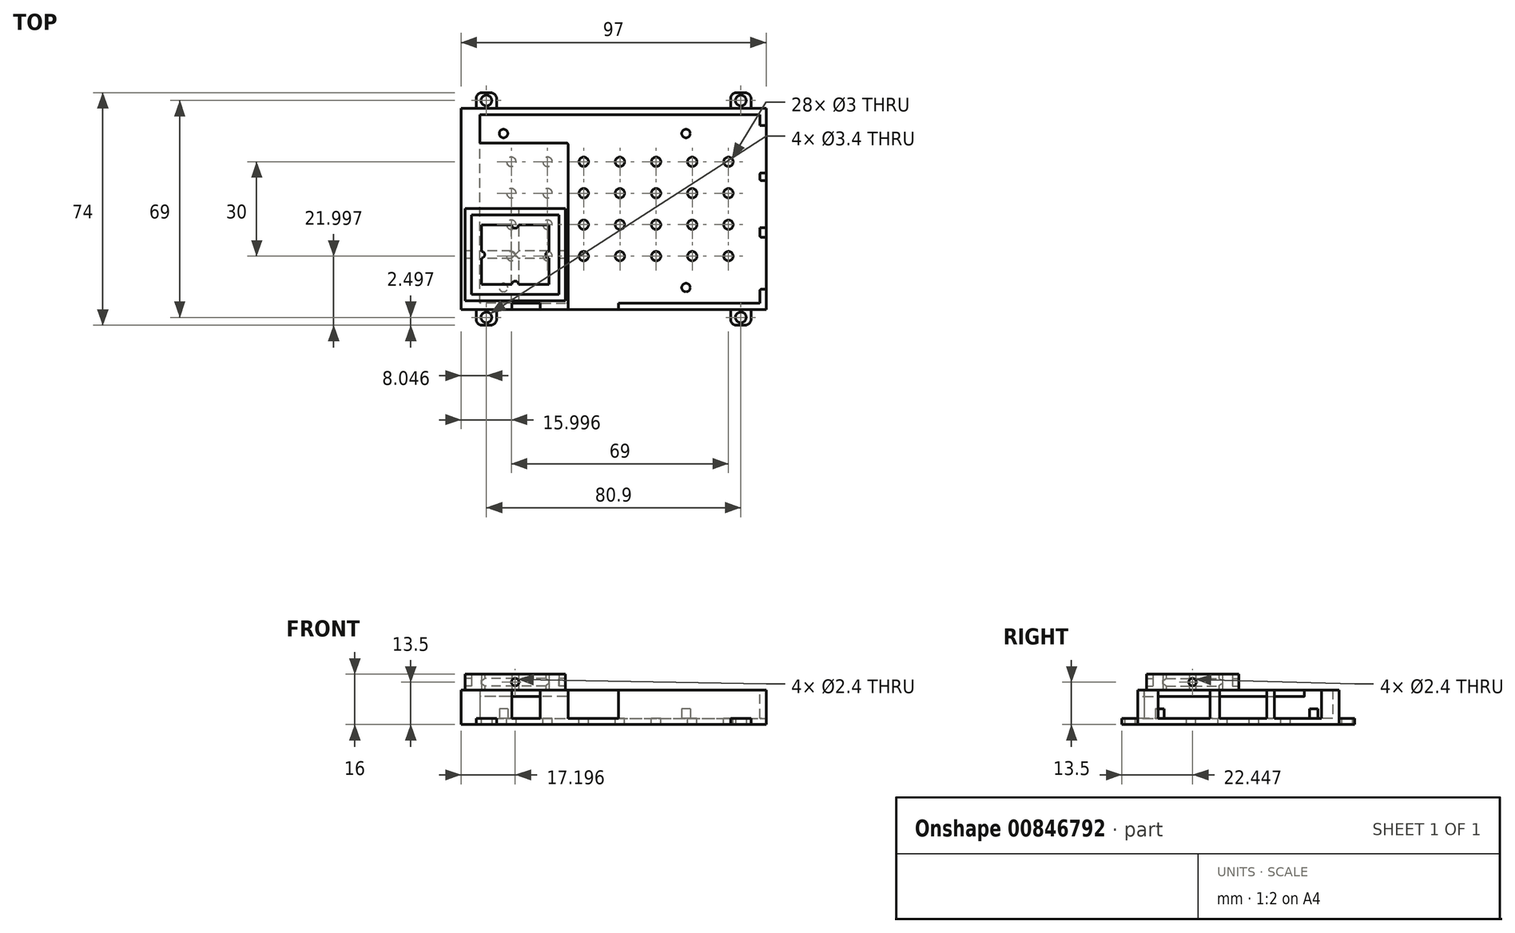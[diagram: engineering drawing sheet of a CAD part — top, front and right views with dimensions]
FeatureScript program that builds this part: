
annotation { "Feature Type Name" : "Feature", "Feature Type Description" : "" }
export const myFeature = defineFeature(function(context is Context, id is Id, definition is map)
    precondition{}
    {
        {
            var Q0;
            Q0=qCreatedBy(makeId("Top.planeOp"),FACE);
            var sketch = newSketch(context, id + "F0", { "sketchPlane" : qUnion([Q0])});
            skLineSegment(sketch, "E0.bottom", {"start": v(-40.08, 52.72) * mm, "end": v(56.92, 52.72) * mm});
            skLineSegment(sketch, "E0.top", {"start": v(-40.08, -11.28) * mm, "end": v(56.92, -11.28) * mm});
            skLineSegment(sketch, "E0.left", {"start": v(-40.08, 52.72) * mm, "end": v(-40.08, -11.28) * mm});
            skLineSegment(sketch, "E0.right", {"start": v(56.92, 52.72) * mm, "end": v(56.92, -11.28) * mm});
            skLineSegment(sketch, "E1", {"start": v(-34.08, 52.72) * mm, "end": v(-34.08, -11.28) * mm});
            skLineSegment(sketch, "E2", {"start": v(-40.08, -9.28) * mm, "end": v(56.92, -9.28) * mm});
            skLineSegment(sketch, "E3", {"start": v(54.92, -11.28) * mm, "end": v(54.92, 52.72) * mm});
            skLineSegment(sketch, "E4", {"start": v(-40.08, 50.72) * mm, "end": v(56.92, 50.72) * mm});
            skCircle(sketch, "E5", {"center": v(-26.58, 44.72) * mm, "radius": 1.35 * mm});
            skCircle(sketch, "E6", {"center": v(31.42, 44.72) * mm, "radius": 1.35 * mm});
            skCircle(sketch, "E7", {"center": v(31.42, -4.28) * mm, "radius": 1.35 * mm});
            skCircle(sketch, "E8", {"center": v(-26.58, -4.28) * mm, "radius": 1.35 * mm});
            skSolve(sketch);
        }
        {
            var Q0;
            {var subQ0=sQuery(id+"F0.wireOp",EDGE,"E2");var subQ1=sQuery(id+"F0.wireOp",EDGE,"E0.left");var subQ2=makeQuery(id+"F0.imprint","INTERSECT",VERTEX,{"derivedFrom":[subQ1,subQ0]});Q0=makeQuery(id+"F0.imprint","IMPRINT",FACE,{"disambiguationData":[TD([[makeQuery(id+"F0.imprint","IMPRINT",EDGE,{"disambiguationData":[TD([[subQ2,1.0]])],"derivedFrom":subQ1}),1.0]])]});}
            var Q1;
            {var subQ0=sQuery(id+"F0.wireOp",EDGE,"E1");var subQ1=sQuery(id+"F0.wireOp",EDGE,"E0.bottom");var subQ2=makeQuery(id+"F0.imprint","INTERSECT",VERTEX,{"derivedFrom":[subQ1,subQ0]});Q1=makeQuery(id+"F0.imprint","IMPRINT",FACE,{"disambiguationData":[TD([[makeQuery(id+"F0.imprint","IMPRINT",EDGE,{"disambiguationData":[TD([[subQ2,-1.0]])],"derivedFrom":subQ1}),-1.0]])]});}
            var Q2;
            {var subQ0=sQuery(id+"F0.wireOp",EDGE,"E1");var subQ1=sQuery(id+"F0.wireOp",EDGE,"E0.top");var subQ2=makeQuery(id+"F0.imprint","INTERSECT",VERTEX,{"derivedFrom":[subQ1,subQ0]});Q2=makeQuery(id+"F0.imprint","IMPRINT",FACE,{"disambiguationData":[TD([[makeQuery(id+"F0.imprint","IMPRINT",EDGE,{"disambiguationData":[TD([[subQ2,-1.0]])],"derivedFrom":subQ1}),1.0]])]});}
            var Q3;
            {var subQ0=sQuery(id+"F0.wireOp",EDGE,"E0.left");var subQ1=sQuery(id+"F0.wireOp",EDGE,"E0.top");var subQ2=makeQuery(id+"F0.imprint","INTERSECT",VERTEX,{"derivedFrom":[subQ1,subQ0]});Q3=makeQuery(id+"F0.imprint","IMPRINT",FACE,{"disambiguationData":[TD([[makeQuery(id+"F0.imprint","IMPRINT",EDGE,{"disambiguationData":[TD([[subQ2,-1.0]])],"derivedFrom":subQ1}),1.0]])]});}
            var Q4;
            {var subQ0=sQuery(id+"F0.wireOp",EDGE,"E0.left");var subQ1=sQuery(id+"F0.wireOp",EDGE,"E0.bottom");var subQ2=makeQuery(id+"F0.imprint","INTERSECT",VERTEX,{"derivedFrom":[subQ1,subQ0]});Q4=makeQuery(id+"F0.imprint","IMPRINT",FACE,{"disambiguationData":[TD([[makeQuery(id+"F0.imprint","IMPRINT",EDGE,{"disambiguationData":[TD([[subQ2,-1.0]])],"derivedFrom":subQ1}),-1.0]])]});}
            var Q5;
            {var subQ0=sQuery(id+"F0.wireOp",EDGE,"E0.right");var subQ1=sQuery(id+"F0.wireOp",EDGE,"E0.bottom");var subQ2=makeQuery(id+"F0.imprint","INTERSECT",VERTEX,{"derivedFrom":[subQ1,subQ0]});Q5=makeQuery(id+"F0.imprint","IMPRINT",FACE,{"disambiguationData":[TD([[makeQuery(id+"F0.imprint","IMPRINT",EDGE,{"disambiguationData":[TD([[subQ2,1.0]])],"derivedFrom":subQ1}),-1.0]])]});}
            var Q6;
            {var subQ0=sQuery(id+"F0.wireOp",EDGE,"E2");var subQ1=sQuery(id+"F0.wireOp",EDGE,"E0.right");var subQ2=makeQuery(id+"F0.imprint","INTERSECT",VERTEX,{"derivedFrom":[subQ1,subQ0]});Q6=makeQuery(id+"F0.imprint","IMPRINT",FACE,{"disambiguationData":[TD([[makeQuery(id+"F0.imprint","IMPRINT",EDGE,{"disambiguationData":[TD([[subQ2,1.0]])],"derivedFrom":subQ1}),-1.0]])]});}
            var Q7;
            {var subQ0=sQuery(id+"F0.wireOp",EDGE,"E0.right");var subQ1=sQuery(id+"F0.wireOp",EDGE,"E0.top");var subQ2=makeQuery(id+"F0.imprint","INTERSECT",VERTEX,{"derivedFrom":[subQ1,subQ0]});Q7=makeQuery(id+"F0.imprint","IMPRINT",FACE,{"disambiguationData":[TD([[makeQuery(id+"F0.imprint","IMPRINT",EDGE,{"disambiguationData":[TD([[subQ2,1.0]])],"derivedFrom":subQ1}),1.0]])]});}
            extrude(context, id + "F1", {"entities" : qUnion([Q0, Q1, Q2, Q3, Q4, Q5, Q6, Q7]), "depth" : 11 * mm, "offsetDistance" : 25 * mm});
        }
        {
            var Q0;
            {var subQ0=sQuery(id+"F0.wireOp",EDGE,"E4");var subQ1=sQuery(id+"F0.wireOp",EDGE,"E1");var subQ2=makeQuery(id+"F0.imprint","INTERSECT",VERTEX,{"derivedFrom":[subQ1,subQ0]});Q0=makeQuery(id+"F0.imprint","IMPRINT",FACE,{"disambiguationData":[TD([[makeQuery(id+"F0.imprint","IMPRINT",EDGE,{"disambiguationData":[TD([[subQ2,-1.0]])],"derivedFrom":subQ1}),1.0]])]});}
            extrude(context, id + "F2", {"entities" : qUnion([Q0]), "operationType" : NewBodyOperationType.ADD, "depth" : 2 * mm, "offsetDistance" : 25 * mm});
        }
        {
            var Q0;
            Q0=makeQuery(id+"F0.imprint","IMPRINT",FACE,{"disambiguationData":[TD([[makeQuery(id+"F0.imprint","IMPRINT",EDGE,{"derivedFrom":sQuery(id+"F0.wireOp",EDGE,"E8")}),1.0]])]});
            var Q1;
            Q1=makeQuery(id+"F0.imprint","IMPRINT",FACE,{"disambiguationData":[TD([[makeQuery(id+"F0.imprint","IMPRINT",EDGE,{"derivedFrom":sQuery(id+"F0.wireOp",EDGE,"E7")}),1.0]])]});
            var Q2;
            Q2=makeQuery(id+"F0.imprint","IMPRINT",FACE,{"disambiguationData":[TD([[makeQuery(id+"F0.imprint","IMPRINT",EDGE,{"derivedFrom":sQuery(id+"F0.wireOp",EDGE,"E6")}),1.0]])]});
            var Q3;
            Q3=makeQuery(id+"F0.imprint","IMPRINT",FACE,{"disambiguationData":[TD([[makeQuery(id+"F0.imprint","IMPRINT",EDGE,{"derivedFrom":sQuery(id+"F0.wireOp",EDGE,"E5")}),1.0]])]});
            extrude(context, id + "F3", {"entities" : qUnion([Q0, Q1, Q2, Q3]), "operationType" : NewBodyOperationType.ADD, "depth" : 5 * mm, "offsetDistance" : 25 * mm});
        }
        {
            var Q0;
            Q0=makeQuery(id+"F1.opExtrude","SWEPT_FACE",FACE,{"disambiguationData":[OSD([sQuery(id+"F0.wireOp",EDGE,"E0.top")])]});
            var sketch = newSketch(context, id + "F4", { "sketchPlane" : qUnion([Q0])});
            skLineSegment(sketch, "E9.bottom", {"start": v(-23.98, 2) * mm, "end": v(-14.98, 2) * mm});
            skLineSegment(sketch, "E9.top", {"start": v(-23.98, 11) * mm, "end": v(-14.98, 11) * mm});
            skLineSegment(sketch, "E9.left", {"start": v(-23.98, 2) * mm, "end": v(-23.98, 11) * mm});
            skLineSegment(sketch, "E9.right", {"start": v(-14.98, 2) * mm, "end": v(-14.98, 11) * mm});
            skLineSegment(sketch, "E10.bottom", {"start": v(9.92, 11) * mm, "end": v(-6.08, 11) * mm});
            skLineSegment(sketch, "E10.top", {"start": v(9.92, 2) * mm, "end": v(-6.08, 2) * mm});
            skLineSegment(sketch, "E10.left", {"start": v(9.92, 11) * mm, "end": v(9.92, 2) * mm});
            skLineSegment(sketch, "E10.right", {"start": v(-6.08, 11) * mm, "end": v(-6.08, 2) * mm});
            skPoint(sketch, "E10.middle", {"position": v(1.92, 6.5) * mm});
            skPoint(sketch, "E11", {"position": v(-19.48, 2) * mm});
            skSolve(sketch);
        }
        {
            var Q0;
            Q0=makeQuery(id+"F4.imprint","IMPRINT",FACE,{"disambiguationData":[TD([[makeQuery(id+"F4.imprint","IMPRINT",EDGE,{"derivedFrom":sQuery(id+"F4.wireOp",EDGE,"E9.bottom")}),1.0]])]});
            var Q1;
            Q1=makeQuery(id+"F4.imprint","IMPRINT",FACE,{"disambiguationData":[TD([[makeQuery(id+"F4.imprint","IMPRINT",EDGE,{"derivedFrom":sQuery(id+"F4.wireOp",EDGE,"E10.bottom")}),-1.0]])]});
            extrude(context, id + "F5", {"entities" : qUnion([Q0, Q1]), "operationType" : NewBodyOperationType.REMOVE, "endBound" : BoundingType.UP_TO_NEXT, "oppositeDirection" : true, "depth" : 25 * mm, "offsetDistance" : 25 * mm});
        }
        {
            var Q0;
            Q0=makeQuery(id+"F1.opExtrude","SWEPT_FACE",FACE,{"disambiguationData":[OSD([sQuery(id+"F0.wireOp",EDGE,"E0.right")])]});
            var sketch = newSketch(context, id + "F6", { "sketchPlane" : qUnion([Q0])});
            skPoint(sketch, "E12", {"position": v(-4.78, 2) * mm});
            skPoint(sketch, "E13", {"position": v(11.72, 2) * mm});
            skLineSegment(sketch, "E14.bottom", {"start": v(-4.78, 2) * mm, "end": v(11.72, 2) * mm});
            skLineSegment(sketch, "E14.top", {"start": v(-4.78, 11) * mm, "end": v(11.72, 11) * mm});
            skLineSegment(sketch, "E14.left", {"start": v(-4.78, 2) * mm, "end": v(-4.78, 11) * mm});
            skLineSegment(sketch, "E14.right", {"start": v(11.72, 2) * mm, "end": v(11.72, 11) * mm});
            skPoint(sketch, "E15", {"position": v(22.22, 6.5) * mm});
            skLineSegment(sketch, "E16.bottom", {"start": v(29.72, 11) * mm, "end": v(14.72, 11) * mm});
            skLineSegment(sketch, "E16.top", {"start": v(29.72, 2) * mm, "end": v(14.72, 2) * mm});
            skLineSegment(sketch, "E16.left", {"start": v(29.72, 11) * mm, "end": v(29.72, 2) * mm});
            skLineSegment(sketch, "E16.right", {"start": v(14.72, 11) * mm, "end": v(14.72, 2) * mm});
            skPoint(sketch, "E17", {"position": v(39.72, 6.5) * mm});
            skLineSegment(sketch, "E18.bottom", {"start": v(47.22, 11) * mm, "end": v(32.22, 11) * mm});
            skLineSegment(sketch, "E18.top", {"start": v(47.22, 2) * mm, "end": v(32.22, 2) * mm});
            skLineSegment(sketch, "E18.left", {"start": v(47.22, 11) * mm, "end": v(47.22, 2) * mm});
            skLineSegment(sketch, "E18.right", {"start": v(32.22, 11) * mm, "end": v(32.22, 2) * mm});
            skPoint(sketch, "E19", {"position": v(3.47, 11) * mm});
            skSolve(sketch);
        }
        {
            var Q0;
            Q0=makeQuery(id+"F6.imprint","IMPRINT",FACE,{"disambiguationData":[TD([[makeQuery(id+"F6.imprint","IMPRINT",EDGE,{"derivedFrom":sQuery(id+"F6.wireOp",EDGE,"E14.bottom")}),1.0]])]});
            var Q1;
            Q1=makeQuery(id+"F6.imprint","IMPRINT",FACE,{"disambiguationData":[TD([[makeQuery(id+"F6.imprint","IMPRINT",EDGE,{"derivedFrom":sQuery(id+"F6.wireOp",EDGE,"E16.bottom")}),1.0]])]});
            var Q2;
            Q2=makeQuery(id+"F6.imprint","IMPRINT",FACE,{"disambiguationData":[TD([[makeQuery(id+"F6.imprint","IMPRINT",EDGE,{"derivedFrom":sQuery(id+"F6.wireOp",EDGE,"E18.bottom")}),1.0]])]});
            extrude(context, id + "F7", {"entities" : qUnion([Q0, Q1, Q2]), "operationType" : NewBodyOperationType.REMOVE, "endBound" : BoundingType.UP_TO_NEXT, "oppositeDirection" : true, "depth" : 25 * mm, "offsetDistance" : 25 * mm});
        }
        {
            var Q0;
            {var subQ0=sQuery(id+"F0.wireOp",EDGE,"E2");var subQ1=sQuery(id+"F0.wireOp",EDGE,"E0.left");var subQ2=makeQuery(id+"F0.imprint","INTERSECT",VERTEX,{"derivedFrom":[subQ1,subQ0]});Q0=makeQuery(id+"F0.imprint","IMPRINT",FACE,{"disambiguationData":[TD([[makeQuery(id+"F0.imprint","IMPRINT",EDGE,{"disambiguationData":[TD([[subQ2,1.0]])],"derivedFrom":subQ1}),1.0]])]});}
            var Q1;
            {var subQ0=sQuery(id+"F0.wireOp",EDGE,"E0.left");var subQ1=sQuery(id+"F0.wireOp",EDGE,"E0.bottom");var subQ2=makeQuery(id+"F0.imprint","INTERSECT",VERTEX,{"derivedFrom":[subQ1,subQ0]});Q1=makeQuery(id+"F0.imprint","IMPRINT",FACE,{"disambiguationData":[TD([[makeQuery(id+"F0.imprint","IMPRINT",EDGE,{"disambiguationData":[TD([[subQ2,-1.0]])],"derivedFrom":subQ1}),-1.0]])]});}
            var Q2;
            {var subQ0=sQuery(id+"F0.wireOp",EDGE,"E0.left");var subQ1=sQuery(id+"F0.wireOp",EDGE,"E0.top");var subQ2=makeQuery(id+"F0.imprint","INTERSECT",VERTEX,{"derivedFrom":[subQ1,subQ0]});Q2=makeQuery(id+"F0.imprint","IMPRINT",FACE,{"disambiguationData":[TD([[makeQuery(id+"F0.imprint","IMPRINT",EDGE,{"disambiguationData":[TD([[subQ2,-1.0]])],"derivedFrom":subQ1}),1.0]])]});}
            extrude(context, id + "F8", {"entities" : qUnion([Q0, Q1, Q2]), "operationType" : NewBodyOperationType.ADD, "depth" : 8 * mm, "offsetDistance" : 25 * mm});
        }
        {
            var Q0;
            Q0=makeQuery(id+"F1.opExtrude","SWEPT_FACE",FACE,{"disambiguationData":[OSD([sQuery(id+"F0.wireOp",EDGE,"E1")])]});
            var sketch = newSketch(context, id + "F9", { "sketchPlane" : qUnion([Q0])});
            skLineSegment(sketch, "E20.bottom", {"start": v(-9.28, 11) * mm, "end": v(41.72, 11) * mm});
            skLineSegment(sketch, "E20.top", {"start": v(-9.28, 9) * mm, "end": v(41.72, 9) * mm});
            skLineSegment(sketch, "E20.left", {"start": v(-9.28, 11) * mm, "end": v(-9.28, 9) * mm});
            skLineSegment(sketch, "E20.right", {"start": v(41.72, 11) * mm, "end": v(41.72, 9) * mm});
            skSolve(sketch);
        }
        {
            var Q0;
            Q0=makeQuery(id+"F9.imprint","IMPRINT",FACE,{"disambiguationData":[TD([[makeQuery(id+"F9.imprint","IMPRINT",EDGE,{"derivedFrom":sQuery(id+"F9.wireOp",EDGE,"E20.bottom")}),1.0]])]});
            extrude(context, id + "F10", {"entities" : qUnion([Q0]), "operationType" : NewBodyOperationType.ADD, "depth" : 28 * mm, "offsetDistance" : 25 * mm});
        }
        {
            var Q0;
            {var subQ0=sQuery(id+"F0.wireOp",EDGE,"E8");var subQ1=sQuery(id+"F0.wireOp",EDGE,"E7");var subQ2=sQuery(id+"F0.wireOp",EDGE,"E6");var subQ3=sQuery(id+"F0.wireOp",EDGE,"E5");var subQ4=sQuery(id+"F0.wireOp",EDGE,"E4");var subQ5=sQuery(id+"F0.wireOp",EDGE,"E3");var subQ6=sQuery(id+"F0.wireOp",EDGE,"E2");var subQ7=sQuery(id+"F0.wireOp",EDGE,"E1");Q0=makeQuery(id+"F3.boolean.opBoolean","MERGE",FACE,{"derivedFrom":[makeQuery(id+"F2.boolean.opBoolean","MERGE",FACE,{"derivedFrom":[makeQuery(id+"F1.opExtrude","CAP_FACE",FACE,{"disambiguationData":[OSD([sQuery(id+"F0.wireOp",EDGE,"E0.bottom"),sQuery(id+"F0.wireOp",EDGE,"E0.top"),sQuery(id+"F0.wireOp",EDGE,"E0.left"),sQuery(id+"F0.wireOp",EDGE,"E0.right"),subQ7,subQ6,subQ5,subQ4])],"isStart":true}),makeQuery(id+"F2.opExtrude","CAP_FACE",FACE,{"disambiguationData":[OSD([subQ7,subQ6,subQ5,subQ4,subQ3,subQ2,subQ1,subQ0])],"isStart":true})]}),makeQuery(id+"F3.opExtrude","CAP_FACE",FACE,{"disambiguationData":[OSD([subQ3])],"isStart":true}),makeQuery(id+"F3.opExtrude","CAP_FACE",FACE,{"disambiguationData":[OSD([subQ2])],"isStart":true}),makeQuery(id+"F3.opExtrude","CAP_FACE",FACE,{"disambiguationData":[OSD([subQ1])],"isStart":true}),makeQuery(id+"F3.opExtrude","CAP_FACE",FACE,{"disambiguationData":[OSD([subQ0])],"isStart":true})]});}
            var sketch = newSketch(context, id + "F11", { "sketchPlane" : qUnion([Q0])});
            skLineSegment(sketch, "E21.bottom", {"start": v(45.62, 16.28) * mm, "end": v(52.12, 16.28) * mm});
            skLineSegment(sketch, "E21.top", {"start": v(45.62, 9.28) * mm, "end": v(52.12, 9.28) * mm});
            skLineSegment(sketch, "E21.left", {"start": v(52.12, 16.28) * mm, "end": v(52.12, 9.28) * mm});
            skLineSegment(sketch, "E21.right", {"start": v(45.62, 9.28) * mm, "end": v(45.62, 16.28) * mm});
            skLineSegment(sketch, "E22.bottom", {"start": v(45.62, -57.72) * mm, "end": v(52.12, -57.72) * mm});
            skLineSegment(sketch, "E22.top", {"start": v(45.62, -50.72) * mm, "end": v(52.12, -50.72) * mm});
            skLineSegment(sketch, "E22.left", {"start": v(52.12, -57.72) * mm, "end": v(52.12, -50.72) * mm});
            skLineSegment(sketch, "E22.right", {"start": v(45.62, -50.72) * mm, "end": v(45.62, -57.72) * mm});
            skLineSegment(sketch, "E23.bottom", {"start": v(-28.78, -51.22) * mm, "end": v(-35.28, -51.22) * mm});
            skLineSegment(sketch, "E23.top", {"start": v(-28.78, -57.72) * mm, "end": v(-35.28, -57.72) * mm});
            skLineSegment(sketch, "E23.left", {"start": v(-28.78, -57.72) * mm, "end": v(-28.78, -51.22) * mm});
            skLineSegment(sketch, "E23.right", {"start": v(-35.28, -51.22) * mm, "end": v(-35.28, -57.72) * mm});
            skLineSegment(sketch, "E24.bottom", {"start": v(-28.78, 16.28) * mm, "end": v(-35.28, 16.28) * mm});
            skLineSegment(sketch, "E24.top", {"start": v(-28.78, 9.78) * mm, "end": v(-35.28, 9.78) * mm});
            skLineSegment(sketch, "E24.left", {"start": v(-28.78, 16.28) * mm, "end": v(-28.78, 9.78) * mm});
            skLineSegment(sketch, "E24.right", {"start": v(-35.28, 16.28) * mm, "end": v(-35.28, 9.78) * mm});
            skPoint(sketch, "E25", {"position": v(-32.03, 13.78) * mm});
            skPoint(sketch, "E25.positionSnap0", {"position": v(-32.03, 16.28) * mm});
            skPoint(sketch, "E26", {"position": v(48.87, 13.78) * mm});
            skPoint(sketch, "E26.positionSnap0", {"position": v(48.87, 16.28) * mm});
            skPoint(sketch, "E27", {"position": v(48.87, -55.22) * mm});
            skPoint(sketch, "E27.positionSnap0", {"position": v(48.87, -57.72) * mm});
            skPoint(sketch, "E28", {"position": v(-32.03, -55.22) * mm});
            skPoint(sketch, "E28.positionSnap0", {"position": v(-32.03, -57.72) * mm});
            skCircle(sketch, "E29", {"center": v(48.87, 13.78) * mm, "radius": 1.5 * mm});
            skCircle(sketch, "E30", {"center": v(-32.03, 13.78) * mm, "radius": 1.5 * mm});
            skCircle(sketch, "E31", {"center": v(-32.03, -55.22) * mm, "radius": 1.5 * mm});
            skCircle(sketch, "E32", {"center": v(48.87, -55.22) * mm, "radius": 1.5 * mm});
            skSolve(sketch);
        }
        {
            var Q0;
            {var subQ5=sQuery(id+"F11.wireOp",EDGE,"E21.bottom");Q0=makeQuery(id+"F11.imprint","IMPRINT",FACE,{"disambiguationData":[TD([[makeQuery(id+"F11.imprint","IMPRINT",EDGE,{"derivedFrom":subQ5}),-1.0]])]});}
            var Q1;
            {var subQ5=sQuery(id+"F11.wireOp",EDGE,"E22.bottom");Q1=makeQuery(id+"F11.imprint","IMPRINT",FACE,{"disambiguationData":[TD([[makeQuery(id+"F11.imprint","IMPRINT",EDGE,{"derivedFrom":subQ5}),1.0]])]});}
            var Q2;
            {var subQ6=sQuery(id+"F11.wireOp",EDGE,"E23.top");Q2=makeQuery(id+"F11.imprint","IMPRINT",FACE,{"disambiguationData":[TD([[makeQuery(id+"F11.imprint","IMPRINT",EDGE,{"derivedFrom":subQ6}),-1.0]])]});}
            var Q3;
            {var subQ1=sQuery(id+"F11.wireOp",EDGE,"E24.bottom");Q3=makeQuery(id+"F11.imprint","IMPRINT",FACE,{"disambiguationData":[TD([[makeQuery(id+"F11.imprint","IMPRINT",EDGE,{"derivedFrom":subQ1}),1.0]])]});}
            var Q4;
            {var subQ0=sQuery(id+"F11.wireOp",EDGE,"E21.right");var subQ1=sQuery(id+"F11.wireOp",EDGE,"E21.top");var subQ2=makeQuery(id+"F11.imprint","INTERSECT",VERTEX,{"derivedFrom":[subQ1,subQ0]});Q4=makeQuery(id+"F11.imprint","IMPRINT",FACE,{"disambiguationData":[TD([[makeQuery(id+"F11.imprint","IMPRINT",EDGE,{"disambiguationData":[TD([[subQ2,-1.0]])],"derivedFrom":subQ1}),1.0]])]});}
            var Q5;
            {var subQ0=sQuery(id+"F11.wireOp",EDGE,"E22.right");var subQ1=sQuery(id+"F11.wireOp",EDGE,"E22.top");var subQ2=makeQuery(id+"F11.imprint","INTERSECT",VERTEX,{"derivedFrom":[subQ1,subQ0]});Q5=makeQuery(id+"F11.imprint","IMPRINT",FACE,{"disambiguationData":[TD([[makeQuery(id+"F11.imprint","IMPRINT",EDGE,{"disambiguationData":[TD([[subQ2,-1.0]])],"derivedFrom":subQ1}),-1.0]])]});}
            var Q6;
            {var subQ0=sQuery(id+"F11.wireOp",EDGE,"E23.left");var subQ1=sQuery(id+"F11.wireOp",EDGE,"E23.bottom");var subQ2=makeQuery(id+"F11.imprint","INTERSECT",VERTEX,{"derivedFrom":[subQ1,subQ0]});Q6=makeQuery(id+"F11.imprint","IMPRINT",FACE,{"disambiguationData":[TD([[makeQuery(id+"F11.imprint","IMPRINT",EDGE,{"disambiguationData":[TD([[subQ2,-1.0]])],"derivedFrom":subQ1}),1.0]])]});}
            var Q7;
            {var subQ0=sQuery(id+"F11.wireOp",EDGE,"E24.left");var subQ1=sQuery(id+"F11.wireOp",EDGE,"E24.top");var subQ2=makeQuery(id+"F11.imprint","INTERSECT",VERTEX,{"derivedFrom":[subQ1,subQ0]});Q7=makeQuery(id+"F11.imprint","IMPRINT",FACE,{"disambiguationData":[TD([[makeQuery(id+"F11.imprint","IMPRINT",EDGE,{"disambiguationData":[TD([[subQ2,-1.0]])],"derivedFrom":subQ1}),-1.0]])]});}
            var Q8;
            Q8=makeQuery(id+"F11.imprint","IMPRINT",FACE,{"disambiguationData":[TD([[makeQuery(id+"F11.imprint","IMPRINT",EDGE,{"derivedFrom":sQuery(id+"F11.wireOp",EDGE,"E30")}),1.0]])]});
            var Q9;
            Q9=makeQuery(id+"F11.imprint","IMPRINT",FACE,{"disambiguationData":[TD([[makeQuery(id+"F11.imprint","IMPRINT",EDGE,{"derivedFrom":sQuery(id+"F11.wireOp",EDGE,"E31")}),1.0]])]});
            var Q10;
            Q10=makeQuery(id+"F11.imprint","IMPRINT",FACE,{"disambiguationData":[TD([[makeQuery(id+"F11.imprint","IMPRINT",EDGE,{"derivedFrom":sQuery(id+"F11.wireOp",EDGE,"E32")}),1.0]])]});
            var Q11;
            Q11=makeQuery(id+"F11.imprint","IMPRINT",FACE,{"disambiguationData":[TD([[makeQuery(id+"F11.imprint","IMPRINT",EDGE,{"derivedFrom":sQuery(id+"F11.wireOp",EDGE,"E29")}),1.0]])]});
            extrude(context, id + "F12", {"entities" : qUnion([Q0, Q1, Q2, Q3, Q4, Q5, Q6, Q7, Q8, Q9, Q10, Q11]), "operationType" : NewBodyOperationType.ADD, "oppositeDirection" : true, "depth" : 2 * mm, "offsetDistance" : 25 * mm});
        }
        {
            var Q0;
            Q0=makeQuery(id+"F12.opExtrude","SWEPT_EDGE",EDGE,{"disambiguationData":[OSD([sQuery(id+"F11.wireOp",EDGE,"E23.bottom"),sQuery(id+"F11.wireOp",EDGE,"E23.right")])]});
            var Q1;
            Q1=makeQuery(id+"F12.opExtrude","SWEPT_EDGE",EDGE,{"disambiguationData":[OSD([sQuery(id+"F11.wireOp",EDGE,"E23.top"),sQuery(id+"F11.wireOp",EDGE,"E23.left")])]});
            var Q2;
            Q2=makeQuery(id+"F12.opExtrude","SWEPT_EDGE",EDGE,{"disambiguationData":[OSD([sQuery(id+"F11.wireOp",EDGE,"E23.top"),sQuery(id+"F11.wireOp",EDGE,"E23.right")])]});
            var Q3;
            Q3=makeQuery(id+"F12.opExtrude","SWEPT_EDGE",EDGE,{"disambiguationData":[OSD([sQuery(id+"F11.wireOp",EDGE,"E24.top"),sQuery(id+"F11.wireOp",EDGE,"E24.right")])]});
            var Q4;
            Q4=makeQuery(id+"F12.opExtrude","SWEPT_EDGE",EDGE,{"disambiguationData":[OSD([sQuery(id+"F11.wireOp",EDGE,"E24.bottom"),sQuery(id+"F11.wireOp",EDGE,"E24.right")])]});
            var Q5;
            Q5=makeQuery(id+"F12.opExtrude","SWEPT_EDGE",EDGE,{"disambiguationData":[OSD([sQuery(id+"F11.wireOp",EDGE,"E24.bottom"),sQuery(id+"F11.wireOp",EDGE,"E24.left")])]});
            var Q6;
            Q6=makeQuery(id+"F12.opExtrude","SWEPT_EDGE",EDGE,{"disambiguationData":[OSD([sQuery(id+"F11.wireOp",EDGE,"E21.bottom"),sQuery(id+"F11.wireOp",EDGE,"E21.right")])]});
            var Q7;
            Q7=makeQuery(id+"F12.opExtrude","SWEPT_EDGE",EDGE,{"disambiguationData":[OSD([sQuery(id+"F11.wireOp",EDGE,"E21.bottom"),sQuery(id+"F11.wireOp",EDGE,"E21.left")])]});
            var Q8;
            Q8=makeQuery(id+"F12.opExtrude","SWEPT_EDGE",EDGE,{"disambiguationData":[OSD([sQuery(id+"F11.wireOp",EDGE,"E21.top"),sQuery(id+"F11.wireOp",EDGE,"E21.left")])]});
            var Q9;
            Q9=makeQuery(id+"F12.opExtrude","SWEPT_EDGE",EDGE,{"disambiguationData":[OSD([sQuery(id+"F11.wireOp",EDGE,"E22.top"),sQuery(id+"F11.wireOp",EDGE,"E22.left")])]});
            var Q10;
            Q10=makeQuery(id+"F12.opExtrude","SWEPT_EDGE",EDGE,{"disambiguationData":[OSD([sQuery(id+"F11.wireOp",EDGE,"E22.bottom"),sQuery(id+"F11.wireOp",EDGE,"E22.left")])]});
            var Q11;
            Q11=makeQuery(id+"F12.opExtrude","SWEPT_EDGE",EDGE,{"disambiguationData":[OSD([sQuery(id+"F11.wireOp",EDGE,"E22.bottom"),sQuery(id+"F11.wireOp",EDGE,"E22.right")])]});
            var Q12;
            Q12=makeQuery(id+"F12.opExtrude","SWEPT_EDGE",EDGE,{"disambiguationData":[OSD([sQuery(id+"F11.wireOp",EDGE,"E21.top"),sQuery(id+"F11.wireOp",EDGE,"E21.right")])]});
            var Q13;
            Q13=makeQuery(id+"F12.opExtrude","SWEPT_EDGE",EDGE,{"disambiguationData":[OSD([sQuery(id+"F11.wireOp",EDGE,"E22.top"),sQuery(id+"F11.wireOp",EDGE,"E22.right")])]});
            var Q14;
            Q14=makeQuery(id+"F12.opExtrude","SWEPT_EDGE",EDGE,{"disambiguationData":[OSD([sQuery(id+"F11.wireOp",EDGE,"E23.bottom"),sQuery(id+"F11.wireOp",EDGE,"E23.left")])]});
            var Q15;
            Q15=makeQuery(id+"F12.opExtrude","SWEPT_EDGE",EDGE,{"disambiguationData":[OSD([sQuery(id+"F11.wireOp",EDGE,"E24.top"),sQuery(id+"F11.wireOp",EDGE,"E24.left")])]});
            fillet(context, id + "F13", {"entities" : qUnion([Q0, Q1, Q2, Q3, Q4, Q5, Q6, Q7, Q8, Q9, Q10, Q11, Q12, Q13, Q14, Q15]), "radius" : 2 * mm, "tangentPropagation" : true, "allowEdgeOverflow" : false});
        }
        {
            var Q0;
            {var subQ0=sQuery(id+"F0.wireOp",EDGE,"E0.bottom");var subQ1=makeQuery(id+"F1.opExtrude","SWEPT_FACE",FACE,{"disambiguationData":[OSD([subQ0])]});var subQ2=sQuery(id+"F0.wireOp",EDGE,"E4");var subQ4=sQuery(id+"F0.wireOp",EDGE,"E0.left");var subQ6=sQuery(id+"F0.wireOp",EDGE,"E0.top");var subQ8=sQuery(id+"F0.wireOp",EDGE,"E0.right");var subQ9=makeQuery(id+"F1.opExtrude","SWEPT_FACE",FACE,{"disambiguationData":[OSD([subQ8])]});var subQ12=sQuery(id+"F0.wireOp",EDGE,"E1");var subQ14=sQuery(id+"F0.wireOp",EDGE,"E2");var subQ16=sQuery(id+"F0.wireOp",EDGE,"E3");var subQ18=makeQuery(id+"F1.opExtrude","CAP_FACE",FACE,{"disambiguationData":[OSD([subQ0,subQ6,subQ4,subQ8,subQ12,subQ14,subQ16,subQ2])],"isStart":false});var subQ19=makeQuery(id+"F10.boolean.opBoolean","MERGE",FACE,{"derivedFrom":[makeQuery(id+"F5.boolean.opBoolean","SPLIT",FACE,{"disambiguationData":[TD([makeQuery(id+"F5.opExtrude","SWEPT_FACE",FACE,{"disambiguationData":[OSD([sQuery(id+"F4.wireOp",EDGE,"E9.right")])]})])],"derivedFrom":subQ18}),makeQuery(id+"F7.boolean.opBoolean","SPLIT",FACE,{"disambiguationData":[TD([subQ1])],"derivedFrom":makeQuery(id+"F5.boolean.opBoolean","SPLIT",FACE,{"disambiguationData":[TD([subQ1])],"derivedFrom":subQ18})}),makeQuery(id+"F10.opExtrude","SWEPT_FACE",FACE,{"disambiguationData":[OSD([sQuery(id+"F9.wireOp",EDGE,"E20.bottom")])]})]});Q0=makeQuery(id+"F13.opFillet","MERGE",FACE,{"derivedFrom":[makeQuery(id+"F12.boolean.opBoolean","SPLIT",FACE,{"disambiguationData":[TD([subQ9])],"derivedFrom":subQ19}),makeQuery(id+"F12.boolean.opBoolean","SPLIT",FACE,{"disambiguationData":[TD([makeQuery(id+"F12.opExtrude","SWEPT_FACE",FACE,{"disambiguationData":[OSD([sQuery(id+"F11.wireOp",EDGE,"E22.right")])]})])],"derivedFrom":subQ19})]});}
            var sketch = newSketch(context, id + "F14", { "sketchPlane" : qUnion([Q0])});
            skLineSegment(sketch, "E33.bottom", {"start": v(-33.63, -3.28) * mm, "end": v(-12.13, -3.28) * mm});
            skLineSegment(sketch, "E33.top", {"start": v(-33.63, 15.62) * mm, "end": v(-12.13, 15.62) * mm});
            skLineSegment(sketch, "E33.left", {"start": v(-33.63, -3.28) * mm, "end": v(-33.63, 15.62) * mm});
            skLineSegment(sketch, "E33.right", {"start": v(-12.13, -3.28) * mm, "end": v(-12.13, 15.62) * mm});
            skCircle(sketch, "E34", {"center": v(-22.88, -3.28) * mm, "radius": 1.05 * mm});
            skCircle(sketch, "E35", {"center": v(-33.63, 6.17) * mm, "radius": 1.05 * mm});
            skCircle(sketch, "E36", {"center": v(-22.88, 15.62) * mm, "radius": 1.05 * mm});
            skCircle(sketch, "E37", {"center": v(-12.13, 6.17) * mm, "radius": 1.05 * mm});
            skLineSegment(sketch, "E38.bottom", {"start": v(-36.83, -6.48) * mm, "end": v(-8.93, -6.48) * mm});
            skLineSegment(sketch, "E38.top", {"start": v(-36.83, 18.82) * mm, "end": v(-8.93, 18.82) * mm});
            skLineSegment(sketch, "E38.left", {"start": v(-36.83, -6.48) * mm, "end": v(-36.83, 18.82) * mm});
            skLineSegment(sketch, "E38.right", {"start": v(-8.93, -6.48) * mm, "end": v(-8.93, 18.82) * mm});
            skLineSegment(sketch, "E39.bottom", {"start": v(-38.83, -8.48) * mm, "end": v(-6.93, -8.48) * mm});
            skLineSegment(sketch, "E39.top", {"start": v(-38.83, 20.82) * mm, "end": v(-6.93, 20.82) * mm});
            skLineSegment(sketch, "E39.left", {"start": v(-38.83, -8.48) * mm, "end": v(-38.83, 20.82) * mm});
            skLineSegment(sketch, "E39.right", {"start": v(-6.93, -8.48) * mm, "end": v(-6.93, 20.82) * mm});
            skSolve(sketch);
        }
        {
            var Q0;
            {var subQ1=sQuery(id+"F14.wireOp",EDGE,"E33.left");var subQ5=sQuery(id+"F14.wireOp",EDGE,"E33.bottom");var subQ14=makeQuery(id+"F14.imprint","INTERSECT",VERTEX,{"derivedFrom":[subQ5,subQ1]});Q0=makeQuery(id+"F14.imprint","IMPRINT",FACE,{"disambiguationData":[TD([[makeQuery(id+"F14.imprint","IMPRINT",EDGE,{"disambiguationData":[TD([[subQ14,-1.0]])],"derivedFrom":subQ5}),1.0]])]});}
            var Q1;
            Q1=makeQuery(id+"F14.imprint","IMPRINT",FACE,{"disambiguationData":[TD([[makeQuery(id+"F14.imprint","IMPRINT",EDGE,{"derivedFrom":sQuery(id+"F14.wireOp",EDGE,"E38.bottom")}),-1.0]])]});
            extrude(context, id + "F15", {"entities" : qUnion([Q0, Q1]), "operationType" : NewBodyOperationType.ADD, "depth" : 5 * mm, "offsetDistance" : 25 * mm});
        }
        {
            var Q0;
            Q0=makeQuery(id+"F15.boolean.opBoolean","MERGE",FACE,{"derivedFrom":[makeQuery(id+"F1.opExtrude","SWEPT_FACE",FACE,{"disambiguationData":[OSD([sQuery(id+"F0.wireOp",EDGE,"E0.left")])]}),makeQuery(id+"F15.opExtrude","SWEPT_FACE",FACE,{"disambiguationData":[OSD([sQuery(id+"F14.wireOp",EDGE,"E39.left")])]})]});
            var sketch = newSketch(context, id + "F16", { "sketchPlane" : qUnion([Q0])});
            skPoint(sketch, "E40", {"position": v(-6.17, 13.5) * mm});
            skPoint(sketch, "E40.positionSnap0", {"position": v(-6.17, 16) * mm});
            skPoint(sketch, "E40.positionSnap1", {"position": v(-20.82, 13.5) * mm});
            skSolve(sketch);
        }
        {
            var Q0;
            Q0=makeQuery(id+"F15.opExtrude","SWEPT_FACE",FACE,{"disambiguationData":[OSD([sQuery(id+"F14.wireOp",EDGE,"E39.top")])]});
            var sketch = newSketch(context, id + "F17", { "sketchPlane" : qUnion([Q0])});
            skPoint(sketch, "E41.positionSnap1", {"position": v(38.83, 13.5) * mm});
            skPoint(sketch, "E42", {"position": v(22.88, 13.5) * mm});
            skPoint(sketch, "E42.positionSnap0", {"position": v(22.88, 16) * mm});
            skPoint(sketch, "E42.positionSnap1", {"position": v(6.93, 13.5) * mm});
            skSolve(sketch);
        }
        {
            var Q0;
            Q0=makeQuery(id+"F2.opExtrude","CAP_FACE",FACE,{"disambiguationData":[OSD([sQuery(id+"F0.wireOp",EDGE,"E1"),sQuery(id+"F0.wireOp",EDGE,"E2"),sQuery(id+"F0.wireOp",EDGE,"E3"),sQuery(id+"F0.wireOp",EDGE,"E4"),sQuery(id+"F0.wireOp",EDGE,"E5"),sQuery(id+"F0.wireOp",EDGE,"E6"),sQuery(id+"F0.wireOp",EDGE,"E7"),sQuery(id+"F0.wireOp",EDGE,"E8")])],"isStart":false});
            var sketch = newSketch(context, id + "F18", { "sketchPlane" : qUnion([Q0])});
            skCircle(sketch, "E43", {"center": v(44.92, 5.72) * mm, "radius": 1.5 * mm});
            skCircle(sketch, "E44.0.1.0", {"center": v(44.92, 15.72) * mm, "radius": 1.5 * mm});
            skCircle(sketch, "E44.0.2.0", {"center": v(44.92, 25.72) * mm, "radius": 1.5 * mm});
            skCircle(sketch, "E44.0.3.0", {"center": v(44.92, 35.72) * mm, "radius": 1.5 * mm});
            skCircle(sketch, "E44.1.0.0", {"center": v(33.42, 5.72) * mm, "radius": 1.5 * mm});
            skCircle(sketch, "E44.1.1.0", {"center": v(33.42, 15.72) * mm, "radius": 1.5 * mm});
            skCircle(sketch, "E44.1.2.0", {"center": v(33.42, 25.72) * mm, "radius": 1.5 * mm});
            skCircle(sketch, "E44.1.3.0", {"center": v(33.42, 35.72) * mm, "radius": 1.5 * mm});
            skCircle(sketch, "E44.2.0.0", {"center": v(21.92, 5.72) * mm, "radius": 1.5 * mm});
            skCircle(sketch, "E44.2.1.0", {"center": v(21.92, 15.72) * mm, "radius": 1.5 * mm});
            skCircle(sketch, "E44.2.2.0", {"center": v(21.92, 25.72) * mm, "radius": 1.5 * mm});
            skCircle(sketch, "E44.2.3.0", {"center": v(21.92, 35.72) * mm, "radius": 1.5 * mm});
            skCircle(sketch, "E44.3.0.0", {"center": v(10.42, 5.72) * mm, "radius": 1.5 * mm});
            skCircle(sketch, "E44.3.1.0", {"center": v(10.42, 15.72) * mm, "radius": 1.5 * mm});
            skCircle(sketch, "E44.3.2.0", {"center": v(10.42, 25.72) * mm, "radius": 1.5 * mm});
            skCircle(sketch, "E44.3.3.0", {"center": v(10.42, 35.72) * mm, "radius": 1.5 * mm});
            skCircle(sketch, "E44.4.0.0", {"center": v(-1.08, 5.72) * mm, "radius": 1.5 * mm});
            skCircle(sketch, "E44.4.1.0", {"center": v(-1.08, 15.72) * mm, "radius": 1.5 * mm});
            skCircle(sketch, "E44.4.2.0", {"center": v(-1.08, 25.72) * mm, "radius": 1.5 * mm});
            skCircle(sketch, "E44.4.3.0", {"center": v(-1.08, 35.72) * mm, "radius": 1.5 * mm});
            skCircle(sketch, "E44.5.0.0", {"center": v(-12.58, 5.72) * mm, "radius": 1.5 * mm});
            skCircle(sketch, "E44.5.1.0", {"center": v(-12.58, 15.72) * mm, "radius": 1.5 * mm});
            skCircle(sketch, "E44.5.2.0", {"center": v(-12.58, 25.72) * mm, "radius": 1.5 * mm});
            skCircle(sketch, "E44.5.3.0", {"center": v(-12.58, 35.72) * mm, "radius": 1.5 * mm});
            skCircle(sketch, "E44.6.0.0", {"center": v(-24.08, 5.72) * mm, "radius": 1.5 * mm});
            skCircle(sketch, "E44.6.1.0", {"center": v(-24.08, 15.72) * mm, "radius": 1.5 * mm});
            skCircle(sketch, "E44.6.2.0", {"center": v(-24.08, 25.72) * mm, "radius": 1.5 * mm});
            skCircle(sketch, "E44.6.3.0", {"center": v(-24.08, 35.72) * mm, "radius": 1.5 * mm});
            skLineSegment(sketch, "E44.direction1", {"start": v(44.92, 5.72) * mm, "end": v(33.42, 5.72) * mm, "construction": true});
            skLineSegment(sketch, "E44.direction2", {"start": v(44.92, 5.72) * mm, "end": v(44.92, 15.72) * mm, "construction": true});
            skSolve(sketch);
        }
        {
            var Q0;
            Q0=makeQuery(id+"F18.imprint","IMPRINT",FACE,{"disambiguationData":[TD([[makeQuery(id+"F18.imprint","IMPRINT",EDGE,{"derivedFrom":sQuery(id+"F18.wireOp",EDGE,"E43")}),1.0]])]});
            var Q1;
            Q1=makeQuery(id+"F18.imprint","IMPRINT",FACE,{"disambiguationData":[TD([[makeQuery(id+"F18.imprint","IMPRINT",EDGE,{"derivedFrom":sQuery(id+"F18.wireOp",EDGE,"E44.0.1.0")}),1.0]])]});
            var Q2;
            Q2=makeQuery(id+"F18.imprint","IMPRINT",FACE,{"disambiguationData":[TD([[makeQuery(id+"F18.imprint","IMPRINT",EDGE,{"derivedFrom":sQuery(id+"F18.wireOp",EDGE,"E44.0.2.0")}),1.0]])]});
            var Q3;
            Q3=makeQuery(id+"F18.imprint","IMPRINT",FACE,{"disambiguationData":[TD([[makeQuery(id+"F18.imprint","IMPRINT",EDGE,{"derivedFrom":sQuery(id+"F18.wireOp",EDGE,"E44.0.3.0")}),1.0]])]});
            var Q4;
            Q4=makeQuery(id+"F18.imprint","IMPRINT",FACE,{"disambiguationData":[TD([[makeQuery(id+"F18.imprint","IMPRINT",EDGE,{"derivedFrom":sQuery(id+"F18.wireOp",EDGE,"E44.1.3.0")}),1.0]])]});
            var Q5;
            Q5=makeQuery(id+"F18.imprint","IMPRINT",FACE,{"disambiguationData":[TD([[makeQuery(id+"F18.imprint","IMPRINT",EDGE,{"derivedFrom":sQuery(id+"F18.wireOp",EDGE,"E44.1.2.0")}),1.0]])]});
            var Q6;
            Q6=makeQuery(id+"F18.imprint","IMPRINT",FACE,{"disambiguationData":[TD([[makeQuery(id+"F18.imprint","IMPRINT",EDGE,{"derivedFrom":sQuery(id+"F18.wireOp",EDGE,"E44.1.1.0")}),1.0]])]});
            var Q7;
            Q7=makeQuery(id+"F18.imprint","IMPRINT",FACE,{"disambiguationData":[TD([[makeQuery(id+"F18.imprint","IMPRINT",EDGE,{"derivedFrom":sQuery(id+"F18.wireOp",EDGE,"E44.1.0.0")}),1.0]])]});
            var Q8;
            Q8=makeQuery(id+"F18.imprint","IMPRINT",FACE,{"disambiguationData":[TD([[makeQuery(id+"F18.imprint","IMPRINT",EDGE,{"derivedFrom":sQuery(id+"F18.wireOp",EDGE,"E44.2.0.0")}),1.0]])]});
            var Q9;
            Q9=makeQuery(id+"F18.imprint","IMPRINT",FACE,{"disambiguationData":[TD([[makeQuery(id+"F18.imprint","IMPRINT",EDGE,{"derivedFrom":sQuery(id+"F18.wireOp",EDGE,"E44.2.1.0")}),1.0]])]});
            var Q10;
            Q10=makeQuery(id+"F18.imprint","IMPRINT",FACE,{"disambiguationData":[TD([[makeQuery(id+"F18.imprint","IMPRINT",EDGE,{"derivedFrom":sQuery(id+"F18.wireOp",EDGE,"E44.2.2.0")}),1.0]])]});
            var Q11;
            Q11=makeQuery(id+"F18.imprint","IMPRINT",FACE,{"disambiguationData":[TD([[makeQuery(id+"F18.imprint","IMPRINT",EDGE,{"derivedFrom":sQuery(id+"F18.wireOp",EDGE,"E44.2.3.0")}),1.0]])]});
            var Q12;
            Q12=makeQuery(id+"F18.imprint","IMPRINT",FACE,{"disambiguationData":[TD([[makeQuery(id+"F18.imprint","IMPRINT",EDGE,{"derivedFrom":sQuery(id+"F18.wireOp",EDGE,"E44.3.3.0")}),1.0]])]});
            var Q13;
            Q13=makeQuery(id+"F18.imprint","IMPRINT",FACE,{"disambiguationData":[TD([[makeQuery(id+"F18.imprint","IMPRINT",EDGE,{"derivedFrom":sQuery(id+"F18.wireOp",EDGE,"E44.3.2.0")}),1.0]])]});
            var Q14;
            Q14=makeQuery(id+"F18.imprint","IMPRINT",FACE,{"disambiguationData":[TD([[makeQuery(id+"F18.imprint","IMPRINT",EDGE,{"derivedFrom":sQuery(id+"F18.wireOp",EDGE,"E44.3.1.0")}),1.0]])]});
            var Q15;
            Q15=makeQuery(id+"F18.imprint","IMPRINT",FACE,{"disambiguationData":[TD([[makeQuery(id+"F18.imprint","IMPRINT",EDGE,{"derivedFrom":sQuery(id+"F18.wireOp",EDGE,"E44.3.0.0")}),1.0]])]});
            var Q16;
            Q16=makeQuery(id+"F18.imprint","IMPRINT",FACE,{"disambiguationData":[TD([[makeQuery(id+"F18.imprint","IMPRINT",EDGE,{"derivedFrom":sQuery(id+"F18.wireOp",EDGE,"E44.4.0.0")}),1.0]])]});
            var Q17;
            Q17=makeQuery(id+"F18.imprint","IMPRINT",FACE,{"disambiguationData":[TD([[makeQuery(id+"F18.imprint","IMPRINT",EDGE,{"derivedFrom":sQuery(id+"F18.wireOp",EDGE,"E44.4.1.0")}),1.0]])]});
            var Q18;
            Q18=makeQuery(id+"F18.imprint","IMPRINT",FACE,{"disambiguationData":[TD([[makeQuery(id+"F18.imprint","IMPRINT",EDGE,{"derivedFrom":sQuery(id+"F18.wireOp",EDGE,"E44.4.2.0")}),1.0]])]});
            var Q19;
            Q19=makeQuery(id+"F18.imprint","IMPRINT",FACE,{"disambiguationData":[TD([[makeQuery(id+"F18.imprint","IMPRINT",EDGE,{"derivedFrom":sQuery(id+"F18.wireOp",EDGE,"E44.4.3.0")}),1.0]])]});
            var Q20;
            Q20=makeQuery(id+"F18.imprint","IMPRINT",FACE,{"disambiguationData":[TD([[makeQuery(id+"F18.imprint","IMPRINT",EDGE,{"derivedFrom":sQuery(id+"F18.wireOp",EDGE,"E44.5.3.0")}),1.0]])]});
            var Q21;
            Q21=makeQuery(id+"F18.imprint","IMPRINT",FACE,{"disambiguationData":[TD([[makeQuery(id+"F18.imprint","IMPRINT",EDGE,{"derivedFrom":sQuery(id+"F18.wireOp",EDGE,"E44.5.2.0")}),1.0]])]});
            var Q22;
            Q22=makeQuery(id+"F18.imprint","IMPRINT",FACE,{"disambiguationData":[TD([[makeQuery(id+"F18.imprint","IMPRINT",EDGE,{"derivedFrom":sQuery(id+"F18.wireOp",EDGE,"E44.5.1.0")}),1.0]])]});
            var Q23;
            Q23=makeQuery(id+"F18.imprint","IMPRINT",FACE,{"disambiguationData":[TD([[makeQuery(id+"F18.imprint","IMPRINT",EDGE,{"derivedFrom":sQuery(id+"F18.wireOp",EDGE,"E44.5.0.0")}),1.0]])]});
            var Q24;
            Q24=makeQuery(id+"F18.imprint","IMPRINT",FACE,{"disambiguationData":[TD([[makeQuery(id+"F18.imprint","IMPRINT",EDGE,{"derivedFrom":sQuery(id+"F18.wireOp",EDGE,"E44.6.1.0")}),1.0]])]});
            var Q25;
            Q25=makeQuery(id+"F18.imprint","IMPRINT",FACE,{"disambiguationData":[TD([[makeQuery(id+"F18.imprint","IMPRINT",EDGE,{"derivedFrom":sQuery(id+"F18.wireOp",EDGE,"E44.6.2.0")}),1.0]])]});
            var Q26;
            Q26=makeQuery(id+"F18.imprint","IMPRINT",FACE,{"disambiguationData":[TD([[makeQuery(id+"F18.imprint","IMPRINT",EDGE,{"derivedFrom":sQuery(id+"F18.wireOp",EDGE,"E44.6.3.0")}),1.0]])]});
            var Q27;
            Q27=makeQuery(id+"F18.imprint","IMPRINT",FACE,{"disambiguationData":[TD([[makeQuery(id+"F18.imprint","IMPRINT",EDGE,{"derivedFrom":sQuery(id+"F18.wireOp",EDGE,"E44.6.0.0")}),1.0]])]});
            extrude(context, id + "F19", {"entities" : qUnion([Q0, Q1, Q2, Q3, Q4, Q5, Q6, Q7, Q8, Q9, Q10, Q11, Q12, Q13, Q14, Q15, Q16, Q17, Q18, Q19, Q20, Q21, Q22, Q23, Q24, Q25, Q26, Q27]), "operationType" : NewBodyOperationType.REMOVE, "endBound" : BoundingType.UP_TO_NEXT, "oppositeDirection" : true, "depth" : 25 * mm, "offsetDistance" : 25 * mm});
        }
        {
            var Q0;
            Q0=makeQuery(id+"F7.boolean.opBoolean","COPY",EDGE,{"derivedFrom":makeQuery(id+"F7.opExtrude","CAP_EDGE",EDGE,{"disambiguationData":[OSD([sQuery(id+"F6.wireOp",EDGE,"E14.right")])],"isStart":true})});
            var Q1;
            Q1=makeQuery(id+"F7.boolean.opBoolean","COPY",EDGE,{"derivedFrom":makeQuery(id+"F7.opExtrude","CAP_EDGE",EDGE,{"disambiguationData":[OSD([sQuery(id+"F6.wireOp",EDGE,"E16.right")])],"isStart":true})});
            var Q2;
            Q2=makeQuery(id+"F7.boolean.opBoolean","COPY",EDGE,{"derivedFrom":makeQuery(id+"F7.opExtrude","CAP_EDGE",EDGE,{"disambiguationData":[OSD([sQuery(id+"F6.wireOp",EDGE,"E16.left")])],"isStart":true})});
            var Q3;
            Q3=makeQuery(id+"F7.boolean.opBoolean","COPY",EDGE,{"derivedFrom":makeQuery(id+"F7.opExtrude","CAP_EDGE",EDGE,{"disambiguationData":[OSD([sQuery(id+"F6.wireOp",EDGE,"E18.right")])],"isStart":true})});
            var Q4;
            Q4=makeQuery(id+"F7.boolean.opBoolean","COPY",EDGE,{"derivedFrom":makeQuery(id+"F7.opExtrude","CAP_EDGE",EDGE,{"disambiguationData":[OSD([sQuery(id+"F6.wireOp",EDGE,"E18.left")])],"isStart":true})});
            var Q5;
            Q5=makeQuery(id+"F5.boolean.opBoolean","COPY",EDGE,{"derivedFrom":makeQuery(id+"F5.opExtrude","CAP_EDGE",EDGE,{"disambiguationData":[OSD([sQuery(id+"F4.wireOp",EDGE,"E10.left")])],"isStart":true})});
            var Q6;
            Q6=makeQuery(id+"F5.boolean.opBoolean","COPY",EDGE,{"derivedFrom":makeQuery(id+"F5.opExtrude","CAP_EDGE",EDGE,{"disambiguationData":[OSD([sQuery(id+"F4.wireOp",EDGE,"E10.right")])],"isStart":true})});
            var Q7;
            Q7=makeQuery(id+"F5.boolean.opBoolean","COPY",EDGE,{"derivedFrom":makeQuery(id+"F5.opExtrude","CAP_EDGE",EDGE,{"disambiguationData":[OSD([sQuery(id+"F4.wireOp",EDGE,"E9.right")])],"isStart":true})});
            var Q8;
            Q8=makeQuery(id+"F5.boolean.opBoolean","COPY",EDGE,{"derivedFrom":makeQuery(id+"F5.opExtrude","CAP_EDGE",EDGE,{"disambiguationData":[OSD([sQuery(id+"F4.wireOp",EDGE,"E9.left")])],"isStart":true})});
            var Q9;
            Q9=makeQuery(id+"F5.boolean.opBoolean","COPY",EDGE,{"derivedFrom":makeQuery(id+"F5.opExtrude","CAP_EDGE",EDGE,{"disambiguationData":[OSD([sQuery(id+"F4.wireOp",EDGE,"E10.left")])],"isStart":false})});
            var Q10;
            Q10=makeQuery(id+"F5.boolean.opBoolean","COPY",EDGE,{"derivedFrom":makeQuery(id+"F5.opExtrude","CAP_EDGE",EDGE,{"disambiguationData":[OSD([sQuery(id+"F4.wireOp",EDGE,"E10.right")])],"isStart":false})});
            var Q11;
            Q11=makeQuery(id+"F7.boolean.opBoolean","COPY",EDGE,{"derivedFrom":makeQuery(id+"F7.opExtrude","CAP_EDGE",EDGE,{"disambiguationData":[OSD([sQuery(id+"F6.wireOp",EDGE,"E14.left")])],"isStart":false})});
            var Q12;
            Q12=makeQuery(id+"F7.boolean.opBoolean","COPY",EDGE,{"derivedFrom":makeQuery(id+"F7.opExtrude","CAP_EDGE",EDGE,{"disambiguationData":[OSD([sQuery(id+"F6.wireOp",EDGE,"E14.right")])],"isStart":false})});
            var Q13;
            Q13=makeQuery(id+"F7.boolean.opBoolean","COPY",EDGE,{"derivedFrom":makeQuery(id+"F7.opExtrude","CAP_EDGE",EDGE,{"disambiguationData":[OSD([sQuery(id+"F6.wireOp",EDGE,"E16.left")])],"isStart":false})});
            var Q14;
            Q14=makeQuery(id+"F7.boolean.opBoolean","COPY",EDGE,{"derivedFrom":makeQuery(id+"F7.opExtrude","CAP_EDGE",EDGE,{"disambiguationData":[OSD([sQuery(id+"F6.wireOp",EDGE,"E18.right")])],"isStart":false})});
            var Q15;
            Q15=makeQuery(id+"F7.boolean.opBoolean","COPY",EDGE,{"derivedFrom":makeQuery(id+"F7.opExtrude","CAP_EDGE",EDGE,{"disambiguationData":[OSD([sQuery(id+"F6.wireOp",EDGE,"E18.left")])],"isStart":false})});
            var Q16;
            {var subQ0=sQuery(id+"F4.wireOp",EDGE,"E9.left");Q16=makeQuery(id+"F10.boolean.opBoolean","SPLIT",EDGE,{"disambiguationData":[topologyDisambiguationEdgeConnected([makeQuery(id+"F1.opExtrude","SWEPT_FACE",FACE,{"disambiguationData":[OSD([sQuery(id+"F0.wireOp",EDGE,"E2")])]})])],"derivedFrom":makeQuery(id+"F5.boolean.opBoolean","COPY",EDGE,{"derivedFrom":makeQuery(id+"F5.opExtrude","CAP_EDGE",EDGE,{"disambiguationData":[OSD([subQ0])],"isStart":false})})});}
            var Q17;
            {var subQ0=sQuery(id+"F4.wireOp",EDGE,"E9.right");Q17=makeQuery(id+"F10.boolean.opBoolean","SPLIT",EDGE,{"disambiguationData":[topologyDisambiguationEdgeConnected([makeQuery(id+"F1.opExtrude","SWEPT_FACE",FACE,{"disambiguationData":[OSD([sQuery(id+"F0.wireOp",EDGE,"E2")])]})])],"derivedFrom":makeQuery(id+"F5.boolean.opBoolean","COPY",EDGE,{"derivedFrom":makeQuery(id+"F5.opExtrude","CAP_EDGE",EDGE,{"disambiguationData":[OSD([subQ0])],"isStart":false})})});}
            var Q18;
            Q18=makeQuery(id+"F5.boolean.opBoolean","COPY",EDGE,{"derivedFrom":makeQuery(id+"F5.opExtrude","CAP_EDGE",EDGE,{"disambiguationData":[OSD([sQuery(id+"F4.wireOp",EDGE,"E10.top")])],"isStart":true})});
            var Q19;
            Q19=makeQuery(id+"F5.boolean.opBoolean","COPY",EDGE,{"derivedFrom":makeQuery(id+"F5.opExtrude","CAP_EDGE",EDGE,{"disambiguationData":[OSD([sQuery(id+"F4.wireOp",EDGE,"E10.top")])],"isStart":false})});
            var Q20;
            Q20=makeQuery(id+"F7.boolean.opBoolean","COPY",EDGE,{"derivedFrom":makeQuery(id+"F7.opExtrude","CAP_EDGE",EDGE,{"disambiguationData":[OSD([sQuery(id+"F6.wireOp",EDGE,"E14.bottom")])],"isStart":true})});
            var Q21;
            Q21=makeQuery(id+"F7.boolean.opBoolean","COPY",EDGE,{"derivedFrom":makeQuery(id+"F7.opExtrude","CAP_EDGE",EDGE,{"disambiguationData":[OSD([sQuery(id+"F6.wireOp",EDGE,"E14.bottom")])],"isStart":false})});
            var Q22;
            Q22=makeQuery(id+"F7.boolean.opBoolean","COPY",EDGE,{"derivedFrom":makeQuery(id+"F7.opExtrude","CAP_EDGE",EDGE,{"disambiguationData":[OSD([sQuery(id+"F6.wireOp",EDGE,"E16.top")])],"isStart":false})});
            var Q23;
            Q23=makeQuery(id+"F7.boolean.opBoolean","COPY",EDGE,{"derivedFrom":makeQuery(id+"F7.opExtrude","CAP_EDGE",EDGE,{"disambiguationData":[OSD([sQuery(id+"F6.wireOp",EDGE,"E16.top")])],"isStart":true})});
            var Q24;
            Q24=makeQuery(id+"F7.boolean.opBoolean","COPY",EDGE,{"derivedFrom":makeQuery(id+"F7.opExtrude","CAP_EDGE",EDGE,{"disambiguationData":[OSD([sQuery(id+"F6.wireOp",EDGE,"E18.top")])],"isStart":true})});
            var Q25;
            Q25=makeQuery(id+"F7.boolean.opBoolean","COPY",EDGE,{"derivedFrom":makeQuery(id+"F7.opExtrude","CAP_EDGE",EDGE,{"disambiguationData":[OSD([sQuery(id+"F6.wireOp",EDGE,"E18.top")])],"isStart":false})});
            var Q26;
            Q26=makeQuery(id+"F5.boolean.opBoolean","COPY",EDGE,{"derivedFrom":makeQuery(id+"F5.opExtrude","CAP_EDGE",EDGE,{"disambiguationData":[OSD([sQuery(id+"F4.wireOp",EDGE,"E9.bottom")])],"isStart":true})});
            var Q27;
            Q27=makeQuery(id+"F5.boolean.opBoolean","COPY",EDGE,{"derivedFrom":makeQuery(id+"F5.opExtrude","CAP_EDGE",EDGE,{"disambiguationData":[OSD([sQuery(id+"F4.wireOp",EDGE,"E9.bottom")])],"isStart":false})});
            var Q28;
            Q28=makeQuery(id+"FQP3pljvYVsGctO_1.opFillet","BLEND_EDGE",EDGE,{"blendedFrom":[makeQuery(id+"F1.opExtrude","SWEPT_EDGE",EDGE,{"disambiguationData":[OSD([sQuery(id+"F0.wireOp",EDGE,"E0.top"),sQuery(id+"F0.wireOp",EDGE,"E0.right")])]}),makeQuery(id+"F7.boolean.opBoolean","COPY",FACE,{"derivedFrom":makeQuery(id+"F7.opExtrude","SWEPT_FACE",FACE,{"disambiguationData":[OSD([sQuery(id+"F6.wireOp",EDGE,"E14.left")])]})})],"blendedInto":[makeQuery(id+"F7.boolean.opBoolean","COPY",FACE,{"derivedFrom":makeQuery(id+"F7.opExtrude","SWEPT_FACE",FACE,{"disambiguationData":[OSD([sQuery(id+"F6.wireOp",EDGE,"E14.left")])]})})]});
            var Q29;
            Q29=makeQuery(id+"F10.opExtrude","CAP_EDGE",EDGE,{"disambiguationData":[OSD([sQuery(id+"F9.wireOp",EDGE,"E20.right")])],"isStart":false});
            fillet(context, id + "F20", {"entities" : qUnion([Q0, Q1, Q2, Q3, Q4, Q5, Q6, Q7, Q8, Q9, Q10, Q11, Q12, Q13, Q14, Q15, Q16, Q17, Q18, Q19, Q20, Q21, Q22, Q23, Q24, Q25, Q26, Q27, Q28, Q29]), "radius" : 0.5 * mm, "tangentPropagation" : true, "allowEdgeOverflow" : false});
        }
        {
            var Q0;
            Q0=sQuery(id+"F11.wireOp",VERTEX,"E26");
            var Q1;
            Q1=sQuery(id+"F11.wireOp",VERTEX,"E25");
            var Q2;
            Q2=sQuery(id+"F11.wireOp",VERTEX,"E27");
            var Q3;
            Q3=sQuery(id+"F11.wireOp",VERTEX,"E28");
            var Q4;
            Q4=makeQuery(id+"F1.opExtrude","SWEPT_BODY",BODY,{"disambiguationData":[OSD([sQuery(id+"F0.wireOp",EDGE,"E0.bottom"),sQuery(id+"F0.wireOp",EDGE,"E0.top"),sQuery(id+"F0.wireOp",EDGE,"E0.left"),sQuery(id+"F0.wireOp",EDGE,"E0.right"),sQuery(id+"F0.wireOp",EDGE,"E1"),sQuery(id+"F0.wireOp",EDGE,"E2"),sQuery(id+"F0.wireOp",EDGE,"E3"),sQuery(id+"F0.wireOp",EDGE,"E4")])]});
            hole(context, id + "F21", {"style" : HoleStyle.SIMPLE, "endStyle" : HoleEndStyle.THROUGH, "standardTappedOrClearance" : lookupTablePath({ "fit" : "Normal", "standard" : "ISO", "size" : "M3", "type" : "Clearance" }), "standardBlindInLast" : lookupTablePath({ "fit" : "Normal", "standard" : "ISO", "size" : "M3", "type" : "Clearance" }), "holeDiameter" : 3.4 * mm, "majorDiameter" : 5 * mm, "isTappedThrough" : true, "tappedDepth" : 12 * mm, "tapClearance" : 3, "locations" : qUnion([Q0, Q1, Q2, Q3]), "scope" : qUnion([Q4])});
        }
        {
            var Q0;
            Q0=sQuery(id+"F17.wireOp",VERTEX,"E42");
            var Q1;
            Q1=sQuery(id+"F16.wireOp",VERTEX,"E40");
            var Q2;
            Q2=makeQuery(id+"F1.opExtrude","SWEPT_BODY",BODY,{"disambiguationData":[OSD([sQuery(id+"F0.wireOp",EDGE,"E0.bottom"),sQuery(id+"F0.wireOp",EDGE,"E0.top"),sQuery(id+"F0.wireOp",EDGE,"E0.left"),sQuery(id+"F0.wireOp",EDGE,"E0.right"),sQuery(id+"F0.wireOp",EDGE,"E1"),sQuery(id+"F0.wireOp",EDGE,"E2"),sQuery(id+"F0.wireOp",EDGE,"E3"),sQuery(id+"F0.wireOp",EDGE,"E4")])]});
            hole(context, id + "F22", {"style" : HoleStyle.SIMPLE, "endStyle" : HoleEndStyle.THROUGH, "holeDiameter" : 2.4 * mm, "majorDiameter" : 5 * mm, "isTappedThrough" : true, "tappedDepth" : 12 * mm, "tapClearance" : 3, "locations" : qUnion([Q0, Q1]), "scope" : qUnion([Q2])});
        }
    });
